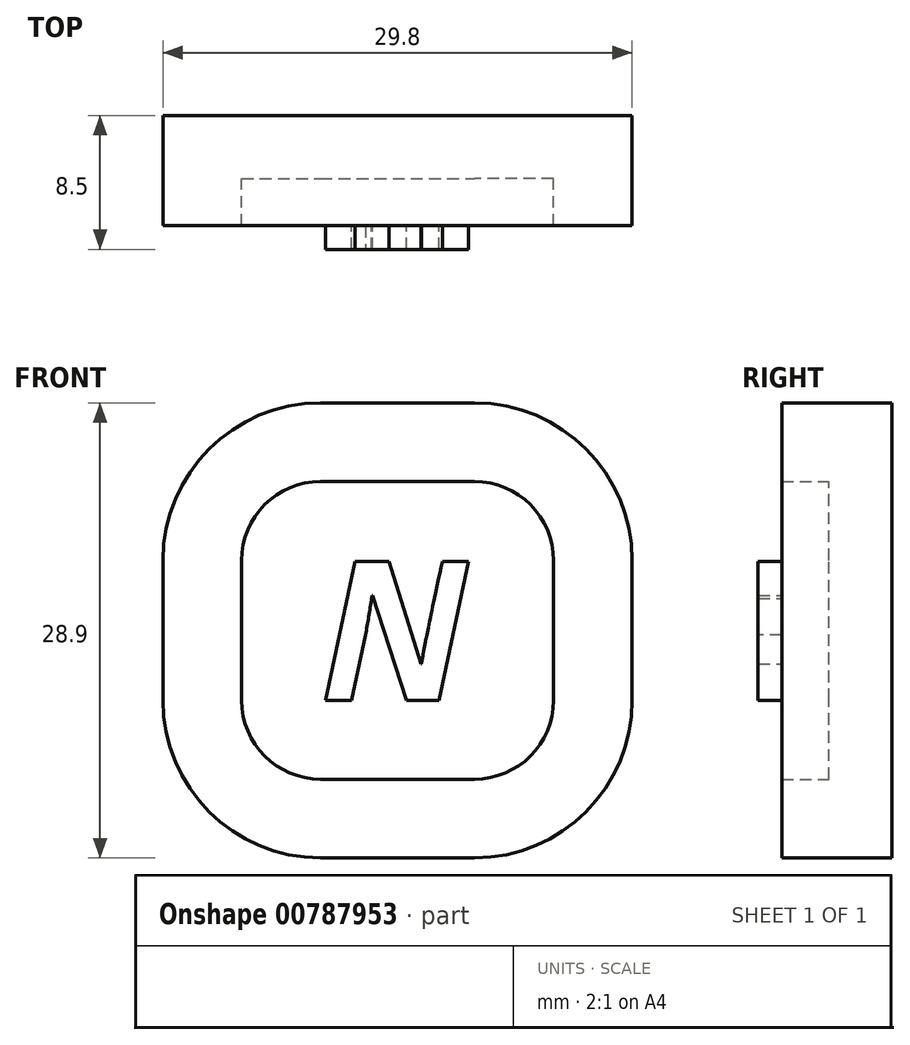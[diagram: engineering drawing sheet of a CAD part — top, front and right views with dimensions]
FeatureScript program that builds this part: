
annotation { "Feature Type Name" : "Feature", "Feature Type Description" : "" }
export const myFeature = defineFeature(function(context is Context, id is Id, definition is map)
    precondition{}
    {
        {
            var Q0;
            Q0=qCreatedBy(makeId("Front.planeOp"),FACE);
            var sketch = newSketch(context, id + "F0", { "sketchPlane" : qUnion([Q0])});
            skLineSegment(sketch, "E0.bottom", {"start": v(-100.56, -15.94) * mm, "end": v(-90.76, -15.94) * mm});
            skLineSegment(sketch, "E0.top", {"start": v(-100.56, 2.96) * mm, "end": v(-90.76, 2.96) * mm});
            skLineSegment(sketch, "E0.left", {"start": v(-105.56, -10.94) * mm, "end": v(-105.56, -2.04) * mm});
            skLineSegment(sketch, "E0.right", {"start": v(-85.76, -10.94) * mm, "end": v(-85.76, -2.04) * mm});
            skPoint(sketch, "E1.visualSharp", {"position": v(-105.56, 2.96) * mm});
            skArc(sketch, "E1.filletArc", {"start": v(-100.56, 2.96) * mm, "mid": v(-104.1, 1.5) * mm, "end": v(-105.56, -2.04) * mm});
            skPoint(sketch, "E2.visualSharp", {"position": v(-85.76, 2.96) * mm});
            skArc(sketch, "E2.filletArc", {"start": v(-85.76, -2.04) * mm, "mid": v(-87.23, 1.5) * mm, "end": v(-90.76, 2.96) * mm});
            skPoint(sketch, "E3.visualSharp", {"position": v(-85.76, -15.94) * mm});
            skArc(sketch, "E3.filletArc", {"start": v(-90.76, -15.94) * mm, "mid": v(-87.23, -14.47) * mm, "end": v(-85.76, -10.94) * mm});
            skPoint(sketch, "E4.visualSharp", {"position": v(-105.56, -15.94) * mm});
            skArc(sketch, "E4.filletArc", {"start": v(-105.56, -10.94) * mm, "mid": v(-104.1, -14.47) * mm, "end": v(-100.56, -15.94) * mm});
            skArc(sketch, "E5.0", {"start": v(-100.56, 7.96) * mm, "mid": v(-107.63, 5.03) * mm, "end": v(-110.56, -2.04) * mm});
            skLineSegment(sketch, "E5.1", {"start": v(-110.56, -10.94) * mm, "end": v(-110.56, -2.04) * mm});
            skLineSegment(sketch, "E5.2", {"start": v(-100.56, 7.96) * mm, "end": v(-90.76, 7.96) * mm});
            skArc(sketch, "E5.3", {"start": v(-110.56, -10.94) * mm, "mid": v(-107.63, -18) * mm, "end": v(-100.56, -20.94) * mm});
            skArc(sketch, "E5.4", {"start": v(-80.76, -2.04) * mm, "mid": v(-83.7, 5.03) * mm, "end": v(-90.76, 7.96) * mm});
            skLineSegment(sketch, "E5.5", {"start": v(-80.76, -10.94) * mm, "end": v(-80.76, -2.04) * mm});
            skArc(sketch, "E5.6", {"start": v(-90.76, -20.94) * mm, "mid": v(-83.7, -18) * mm, "end": v(-80.76, -10.94) * mm});
            skLineSegment(sketch, "E5.7", {"start": v(-100.56, -20.94) * mm, "end": v(-90.76, -20.94) * mm});
            skSolve(sketch);
        }
        {
            var Q0;
            Q0 = qSketchRegion(id + "F0", true);
            extrude(context, id + "F1", {"entities" : qUnion([Q0]), "depth" : 7 * mm, "offsetDistance" : 25 * mm});
        }
        {
            var Q0;
            Q0=makeQuery(id+"F0.imprint","IMPRINT",FACE,{"disambiguationData":[TD([[makeQuery(id+"F0.imprint","IMPRINT",EDGE,{"derivedFrom":sQuery(id+"F0.wireOp",EDGE,"E0.bottom")}),1.0]])]});
            extrude(context, id + "F2", {"entities" : qUnion([Q0]), "operationType" : NewBodyOperationType.ADD, "depth" : 4 * mm, "offsetDistance" : 25 * mm});
        }
        {
            var Q0;
            Q0=makeQuery(id+"F1.opExtrude","CAP_FACE",FACE,{"disambiguationData":[OSD([sQuery(id+"F0.wireOp",EDGE,"E0.bottom"),sQuery(id+"F0.wireOp",EDGE,"E0.top"),sQuery(id+"F0.wireOp",EDGE,"E0.left"),sQuery(id+"F0.wireOp",EDGE,"E0.right"),sQuery(id+"F0.wireOp",EDGE,"E1.filletArc"),sQuery(id+"F0.wireOp",EDGE,"E2.filletArc"),sQuery(id+"F0.wireOp",EDGE,"E3.filletArc"),sQuery(id+"F0.wireOp",EDGE,"E4.filletArc"),sQuery(id+"F0.wireOp",EDGE,"E5.0"),sQuery(id+"F0.wireOp",EDGE,"E5.1"),sQuery(id+"F0.wireOp",EDGE,"E5.2"),sQuery(id+"F0.wireOp",EDGE,"E5.3"),sQuery(id+"F0.wireOp",EDGE,"E5.4"),sQuery(id+"F0.wireOp",EDGE,"E5.5"),sQuery(id+"F0.wireOp",EDGE,"E5.6"),sQuery(id+"F0.wireOp",EDGE,"E5.7")])],"isStart":false});
            var sketch = newSketch(context, id + "F3", { "sketchPlane" : qUnion([Q0])});
            skText(sketch, "E6", { "text": "N", "fontName": "OpenSans-BoldItalic.ttf"});
            const initialGuessF3  = {"E6": [-0.10056, -0.01094, 1, 0, 0.0089]};
            skSetInitialGuess(sketch, initialGuessF3);
            skSolve(sketch);
        }
        {
            var Q0;
            Q0 = qSketchRegion(id + "F3", true);
            extrude(context, id + "F4", {"entities" : qUnion([Q0]), "depth" : 1.5 * mm, "offsetDistance" : 25 * mm});
        }
        {
            var Q0;
            Q0=makeQuery(id+"F1.opExtrude","SWEPT_FACE",FACE,{"disambiguationData":[OSD([sQuery(id+"F0.wireOp",EDGE,"E5.7")])]});
            var sketch = newSketch(context, id + "F5", { "sketchPlane" : qUnion([Q0])});
            skCircle(sketch, "E7", {"center": v(-96.2, -12.5) * mm, "radius": 11.15 * mm});
            skCircle(sketch, "E8", {"center": v(-96.2, -12.5) * mm, "radius": 12.5 * mm});
            skSolve(sketch);
        }
        {
            var Q0;
            Q0 = qSketchRegion(id + "F5", true);
            extrude(context, id + "F6", {"entities" : qUnion([Q0]), "operationType" : NewBodyOperationType.ADD, "oppositeDirection" : true, "depth" : 9 * mm, "offsetDistance" : 25 * mm});
        }
        {
            var Q0;
            Q0=makeQuery(id+"F6.opExtrude","CAP_FACE",FACE,{"disambiguationData":[OSD([sQuery(id+"F5.wireOp",EDGE,"E7"),sQuery(id+"F5.wireOp",EDGE,"L339Q2dJ-5jq2-eKMn-XzOU-F48MwHSq5sYX")])],"isStart":false});
            extrude(context, id + "F7", {"entities" : qUnion([Q0]), "operationType" : NewBodyOperationType.REMOVE, "oppositeDirection" : true, "depth" : 9 * mm, "offsetDistance" : 25 * mm});
        }
        {
            var Q0;
            {var subQ0=sQuery(id+"F5.wireOp",EDGE,"E7");var subQ1=makeQuery(id+"F1.opExtrude","CAP_EDGE",EDGE,{"disambiguationData":[OSD([sQuery(id+"F0.wireOp",EDGE,"E5.7")])],"isStart":true});var subQ2=makeQuery(id+"F5.imprint","INTERSECT",VERTEX,{"disambiguationData":[OD(0.0)],"derivedFrom":[subQ1,subQ0]});Q0=makeQuery(id+"F5.imprint","IMPRINT",FACE,{"disambiguationData":[TD([[makeQuery(id+"F5.imprint","IMPRINT",EDGE,{"disambiguationData":[TD([[subQ2,-1.0]])],"derivedFrom":subQ0}),1.0]])]});}
            extrude(context, id + "F8", {"entities" : qUnion([Q0]), "operationType" : NewBodyOperationType.REMOVE, "oppositeDirection" : true, "depth" : 9 * mm, "offsetDistance" : 25 * mm});
        }
    });
